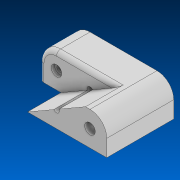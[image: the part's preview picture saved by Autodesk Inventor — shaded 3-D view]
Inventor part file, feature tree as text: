
AUTODESK INVENTOR PART (.ipt)
format: ipt  version: 2022.2 (Build 262287000, 287)  size: 132,608 bytes
history: native  units: in
note: dims shown in document units (in); Inventor stores cm internally (conversion verified against a paired STEP export)
features: extrude x2, hole x2, fillet x2, sketch x1
ambient origin geometry x8: Origin, YZ Plane, XZ Plane, XY Plane, X Axis, Y Axis, Z Axis, Center Point
bodies: Solid1 (feature_tree)
feature tree (7):
  sketch  "Sketch1"  dims[d0=1.0in d1=1.0in d2=1.0in d3=0.5in d4=30.0deg d5=1.0in d6=0.0in d7=1.0in d8=0.0in d9=0.125in d13=0.175in d14=0.75in d15=0.22in d16=0.325in d17=0.5635in d18=1.5in d19=0.0in d20=0.175in d21=0.75in d22=0.315in d23=0.1in d24=0.5635in d25=1.0in d26=0.0in d27=0.5in]
  extrude  "Extrusion1"  Depth=1.0in
  extrude  "Extrusion2"  Depth=1.0in
  hole  "Hole1"  [1 undecoded]
  hole  "Hole2"  [1 undecoded]
  fillet  "Fillet2"  Radius=1.0in
  fillet  "Fillet1"  Radius=1.0in
note: 2 required parameter values undecoded (feature->parameter linkage not recoverable at this tier; creation-order binding heuristic only, values carry confidence <= 0.55)
